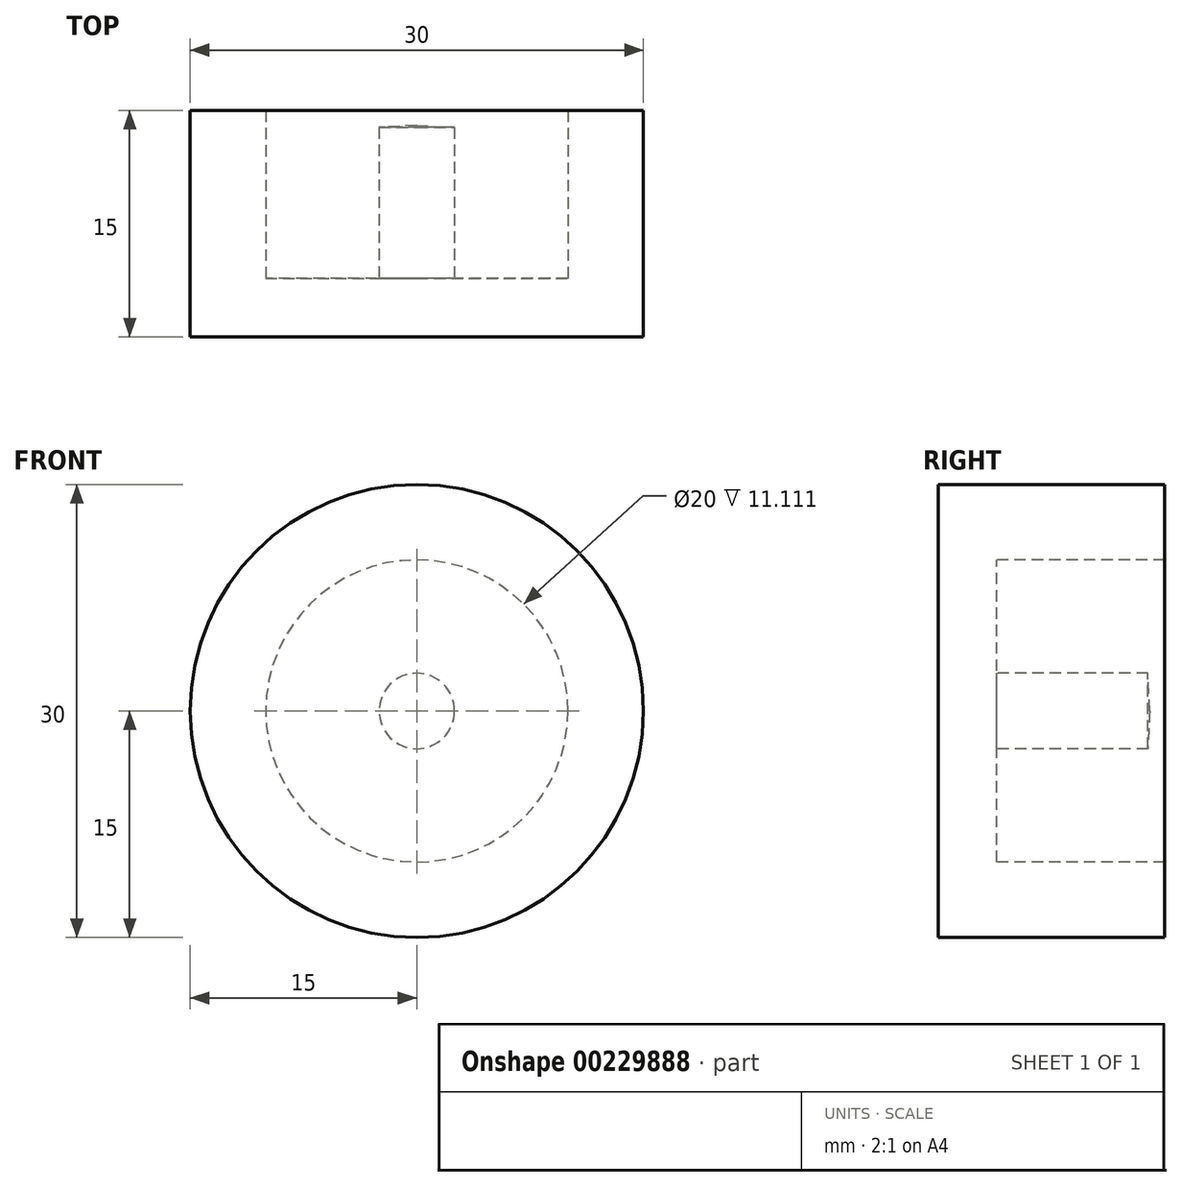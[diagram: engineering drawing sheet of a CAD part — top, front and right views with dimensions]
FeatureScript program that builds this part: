
annotation { "Feature Type Name" : "Feature", "Feature Type Description" : "" }
export const myFeature = defineFeature(function(context is Context, id is Id, definition is map)
    precondition{}
    {
        {
            var Q0;
            Q0=qCreatedBy(makeId("Right.planeOp"),FACE);
            var sketch = newSketch(context, id + "F0", { "sketchPlane" : qUnion([Q0])});
            skLineSegment(sketch, "E0", {"start": v(14, 0) * mm, "end": v(0, 0) * mm});
            skLineSegment(sketch, "E1", {"start": v(0, 0) * mm, "end": v(0, 15) * mm});
            skLineSegment(sketch, "E2", {"start": v(0, 15) * mm, "end": v(15, 15) * mm});
            skLineSegment(sketch, "E3", {"start": v(15, 15) * mm, "end": v(15, 10) * mm});
            skLineSegment(sketch, "E4", {"start": v(15, 10) * mm, "end": v(3.89, 10) * mm});
            skLineSegment(sketch, "E5", {"start": v(3.89, 10) * mm, "end": v(3.89, 2.5) * mm});
            skLineSegment(sketch, "E6", {"start": v(3.89, 2.5) * mm, "end": v(13.89, 2.5) * mm});
            skLineSegment(sketch, "E7", {"start": v(13.89, 2.5) * mm, "end": v(14, 0) * mm});
            skSolve(sketch);
        }
        {
            var Q0;
            Q0=qCreatedBy(makeId("Right.planeOp"),FACE);
            var sketch = newSketch(context, id + "F1", { "sketchPlane" : qUnion([Q0])});
            skLineSegment(sketch, "E8", {"start": v(-75.25, 0) * mm, "end": v(75.36, 0) * mm, "construction": true});
            skSolve(sketch);
        }
        {
            var Q0;
            Q0 = qSketchRegion(id + "F0", true);
            var Q1;
            Q1=sQuery(id+"F1.wireOp",EDGE,"E8");
            revolve(context, id + "F2", {"entities" : qUnion([Q0]), "axis" : qUnion([Q1]), "revolveType" : RevolveType.FULL});
        }
    });
